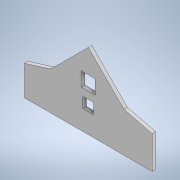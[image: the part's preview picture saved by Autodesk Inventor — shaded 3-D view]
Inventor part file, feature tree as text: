
AUTODESK INVENTOR PART (.ipt)
format: ipt  version: 2020.1 (Build 241239000, 239)  size: 122,880 bytes
history: native  units: in
note: dims shown in document units (in); Inventor stores cm internally (conversion verified against a paired STEP export)
features: extrude x1, sketch x1
ambient origin geometry x8: Origin, YZ Plane, XZ Plane, XY Plane, X Axis, Y Axis, Z Axis, Center Point
bodies: Solid1 (feature_tree)
feature tree (2):
  extrude  "Extrusion1"  Depth=218.0in
  sketch  "Sketch1"  dims[d0=218.0in d1=218.0in d2=102.0in d3=258.0in d4=45.0deg d5=130.0in d6=136.0in d7=45.0deg d8=36.0in d9=36.0in d10=48.0in d11=48.0in d12=12.0in d13=0.0in d14=112.0in d15=94.255in d16=181.0193in d17=172.5341in d18=98.9545in]
